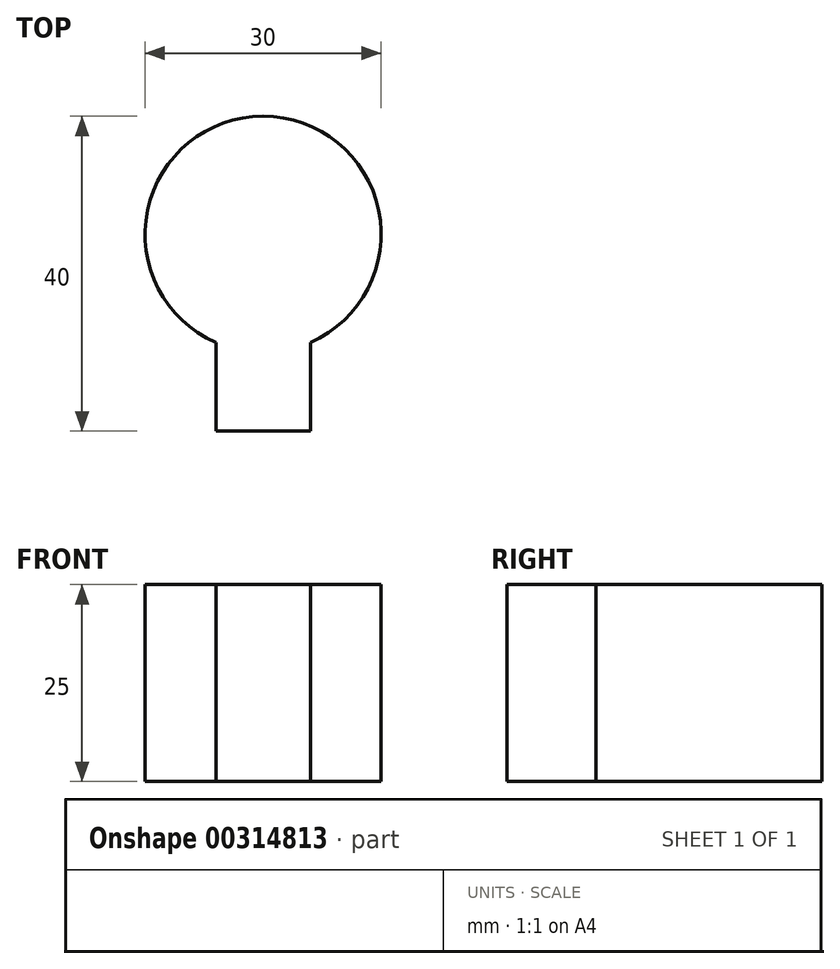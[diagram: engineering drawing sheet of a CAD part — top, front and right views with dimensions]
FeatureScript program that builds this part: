
annotation { "Feature Type Name" : "Feature", "Feature Type Description" : "" }
export const myFeature = defineFeature(function(context is Context, id is Id, definition is map)
    precondition{}
    {
        {
            var Q0;
            Q0=qCreatedBy(makeId("Top.planeOp"),FACE);
            var sketch = newSketch(context, id + "F0", { "sketchPlane" : qUnion([Q0])});
            skArc(sketch, "E0", {"start": v(6, -13.75) * mm, "mid": v(0, 15) * mm, "end": v(-6, -13.75) * mm});
            skLineSegment(sketch, "E1", {"start": v(0, 0) * mm, "end": v(0, -25) * mm, "construction": true});
            skLineSegment(sketch, "E2", {"start": v(0, -25) * mm, "end": v(-6, -25) * mm});
            skLineSegment(sketch, "E3", {"start": v(0, -25) * mm, "end": v(6, -25) * mm});
            skLineSegment(sketch, "E4", {"start": v(-6, -25) * mm, "end": v(-6, -13.75) * mm});
            skLineSegment(sketch, "E5", {"start": v(6, -25) * mm, "end": v(6, -13.75) * mm});
            skSolve(sketch);
        }
        {
            var Q0;
            Q0 = qSketchRegion(id + "F0", true);
            extrude(context, id + "F1", {"entities" : qUnion([Q0]), "depth" : 25 * mm});
        }
    });
